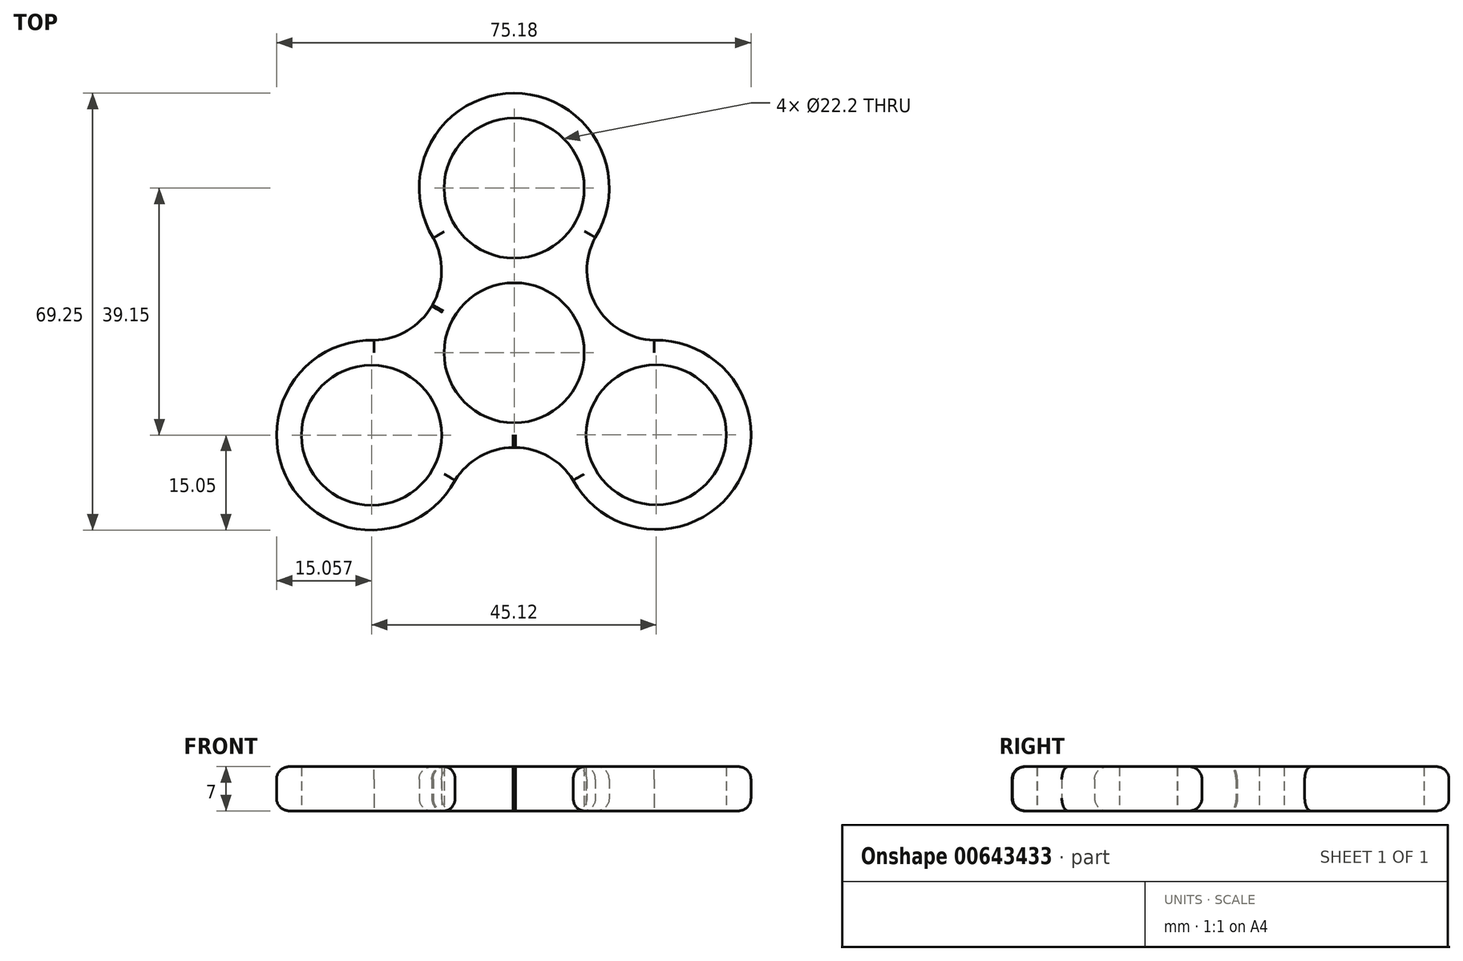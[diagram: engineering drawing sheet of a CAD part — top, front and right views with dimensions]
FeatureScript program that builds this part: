
annotation { "Feature Type Name" : "Feature", "Feature Type Description" : "" }
export const myFeature = defineFeature(function(context is Context, id is Id, definition is map)
    precondition{}
    {
        {
            var Q0;
            Q0=qCreatedBy(makeId("Top.planeOp"),FACE);
            var sketch = newSketch(context, id + "F0", { "sketchPlane" : qUnion([Q0])});
            skPoint(sketch, "E0.0.midPoint", {"position": v(0, -20.2) * mm});
            skCircle(sketch, "E1", {"center": v(0, 0) * mm, "radius": 11.1 * mm});
            skCircle(sketch, "E2", {"center": v(22.52, -13) * mm, "radius": 11.1 * mm});
            skCircle(sketch, "E3", {"center": v(-22.6, -13.05) * mm, "radius": 11.1 * mm});
            skCircle(sketch, "E4", {"center": v(0, 26.1) * mm, "radius": 11.1 * mm});
            skArc(sketch, "E5", {"start": v(-22.18, 2) * mm, "mid": v(-35.64, -20.58) * mm, "end": v(-9.36, -20.2) * mm});
            skArc(sketch, "E6", {"start": v(9.36, -20.2) * mm, "mid": v(35.5, -20.5) * mm, "end": v(22.18, 2) * mm});
            skArc(sketch, "E7", {"start": v(12.86, 18.28) * mm, "mid": v(-0.04, 41.15) * mm, "end": v(-12.82, 18.21) * mm});
            skArc(sketch, "E8", {"start": v(-0.18, -15) * mm, "mid": v(0, -15) * mm, "end": v(0.18, -15) * mm});
            skArc(sketch, "E9", {"start": v(-22.18, 2) * mm, "mid": v(-16.93, 3.52) * mm, "end": v(-13.05, 7.39) * mm});
            skArc(sketch, "E10", {"start": v(9.36, -20.2) * mm, "mid": v(0, -15) * mm, "end": v(-9.36, -20.2) * mm});
            skArc(sketch, "E11", {"start": v(12.86, 18.28) * mm, "mid": v(12.98, 7.54) * mm, "end": v(22.18, 2) * mm});
            skPoint(sketch, "E12.end.orphan", {"position": v(-32.22, -18.6) * mm});
            skArc(sketch, "E13.trimOffspring", {"start": v(-12.93, 7.6) * mm, "mid": v(-13, 7.5) * mm, "end": v(-13.05, 7.39) * mm});
            skPoint(sketch, "E14.end.orphan", {"position": v(-13, -7.5) * mm});
            skPoint(sketch, "E15.orphan", {"position": v(0, 37.2) * mm});
            skPoint(sketch, "E16.end.orphan", {"position": v(0, 15) * mm});
            skArc(sketch, "E17.trimOffspring", {"start": v(-12.93, 7.6) * mm, "mid": v(-11.51, 12.9) * mm, "end": v(-12.82, 18.21) * mm});
            skPoint(sketch, "E18.start.orphan", {"position": v(12.9, -7.45) * mm});
            skPoint(sketch, "E19.start.orphan", {"position": v(-35, -20.2) * mm});
            skPoint(sketch, "E20.trimOffspring.end.orphan", {"position": v(35, -20.2) * mm});
            skPoint(sketch, "E20.trimOffspring.start.orphan", {"position": v(32.13, -18.55) * mm});
            skSolve(sketch);
        }
        {
            var Q0;
            Q0=makeQuery(id+"F0.imprint","IMPRINT",FACE,{"disambiguationData":[TD([[makeQuery(id+"F0.imprint","IMPRINT",EDGE,{"derivedFrom":sQuery(id+"F0.wireOp",EDGE,"E2")}),1.0]])]});
            var Q1;
            Q1=makeQuery(id+"F0.imprint","IMPRINT",FACE,{"disambiguationData":[TD([[makeQuery(id+"F0.imprint","IMPRINT",EDGE,{"derivedFrom":sQuery(id+"F0.wireOp",EDGE,"E1")}),-1.0]])]});
            var Q2;
            Q2=makeQuery(id+"F0.imprint","IMPRINT",FACE,{"disambiguationData":[TD([[makeQuery(id+"F0.imprint","IMPRINT",EDGE,{"derivedFrom":sQuery(id+"F0.wireOp",EDGE,"E4")}),1.0]])]});
            var Q3;
            Q3=makeQuery(id+"F0.imprint","IMPRINT",FACE,{"disambiguationData":[TD([[makeQuery(id+"F0.imprint","IMPRINT",EDGE,{"derivedFrom":sQuery(id+"F0.wireOp",EDGE,"E1")}),1.0]])]});
            var Q4;
            Q4=makeQuery(id+"F0.imprint","IMPRINT",FACE,{"disambiguationData":[TD([[makeQuery(id+"F0.imprint","IMPRINT",EDGE,{"derivedFrom":sQuery(id+"F0.wireOp",EDGE,"E3")}),1.0]])]});
            var Q5;
            {var subQ0=sQuery(id+"F0.wireOp",EDGE,"E8");Q5=makeQuery(id+"F0.imprint","IMPRINT",FACE,{"disambiguationData":[TD([[makeQuery(id+"F0.imprint","IMPRINT",EDGE,{"derivedFrom":subQ0}),1.0]])]});}
            extrude(context, id + "F1", {"entities" : qUnion([Q0, Q1, Q2, Q3, Q4, Q5]), "depth" : 7 * mm, "offsetDistance" : 25 * mm});
        }
        {
            var Q0;
            Q0=makeQuery(id+"F1.opExtrude","CAP_FACE",FACE,{"disambiguationData":[OSD([sQuery(id+"F0.wireOp",EDGE,"E5"),sQuery(id+"F0.wireOp",EDGE,"E6"),sQuery(id+"F0.wireOp",EDGE,"E7"),sQuery(id+"F0.wireOp",EDGE,"E8"),sQuery(id+"F0.wireOp",EDGE,"E9"),sQuery(id+"F0.wireOp",EDGE,"E10"),sQuery(id+"F0.wireOp",EDGE,"E11"),sQuery(id+"F0.wireOp",EDGE,"E13.trimOffspring"),sQuery(id+"F0.wireOp",EDGE,"E17.trimOffspring")])],"isStart":true});
            var Q1;
            Q1=makeQuery(id+"F1.opExtrude","CAP_EDGE",EDGE,{"disambiguationData":[OSD([sQuery(id+"F0.wireOp",EDGE,"E5")])],"isStart":false});
            var Q2;
            Q2=makeQuery(id+"F1.opExtrude","CAP_EDGE",EDGE,{"disambiguationData":[OSD([sQuery(id+"F0.wireOp",EDGE,"E6")])],"isStart":false});
            var Q3;
            Q3=makeQuery(id+"F1.opExtrude","CAP_FACE",FACE,{"disambiguationData":[OSD([sQuery(id+"F0.wireOp",EDGE,"E5"),sQuery(id+"F0.wireOp",EDGE,"E6"),sQuery(id+"F0.wireOp",EDGE,"E7"),sQuery(id+"F0.wireOp",EDGE,"E8"),sQuery(id+"F0.wireOp",EDGE,"E9"),sQuery(id+"F0.wireOp",EDGE,"E10"),sQuery(id+"F0.wireOp",EDGE,"E11"),sQuery(id+"F0.wireOp",EDGE,"E13.trimOffspring"),sQuery(id+"F0.wireOp",EDGE,"E17.trimOffspring")])],"isStart":false});
            fillet(context, id + "F2", {"entities" : qUnion([Q0, Q1, Q2, Q3]), "radius" : 2 * mm, "tangentPropagation" : true, "allowEdgeOverflow" : false});
        }
        {
            var Q0;
            Q0=sQuery(id+"F0.wireOp",VERTEX,"E13.trimOffspring.center");
            var Q1;
            Q1=sQuery(id+"F0.wireOp",VERTEX,"E3.center");
            var Q2;
            Q2=sQuery(id+"F0.wireOp",VERTEX,"E2.center");
            var Q3;
            Q3=sQuery(id+"F0.wireOp",VERTEX,"E4.center");
            var Q4;
            Q4=makeQuery(id+"F1.opExtrude","SWEPT_BODY",BODY,{"disambiguationData":[OSD([sQuery(id+"F0.wireOp",EDGE,"E5"),sQuery(id+"F0.wireOp",EDGE,"E6"),sQuery(id+"F0.wireOp",EDGE,"E7"),sQuery(id+"F0.wireOp",EDGE,"E8"),sQuery(id+"F0.wireOp",EDGE,"E9"),sQuery(id+"F0.wireOp",EDGE,"E10"),sQuery(id+"F0.wireOp",EDGE,"E11"),sQuery(id+"F0.wireOp",EDGE,"E13.trimOffspring"),sQuery(id+"F0.wireOp",EDGE,"E17.trimOffspring")])]});
            hole(context, id + "F3", {"style" : HoleStyle.SIMPLE, "endStyle" : HoleEndStyle.THROUGH, "oppositeDirection" : true, "holeDiameter" : 22.2 * mm, "majorDiameter" : 5 * mm, "isTappedThrough" : true, "tappedDepth" : 12 * mm, "tapClearance" : 3, "startFromSketch" : true, "locations" : qUnion([Q0, Q1, Q2, Q3]), "scope" : qUnion([Q4])});
        }
    });
